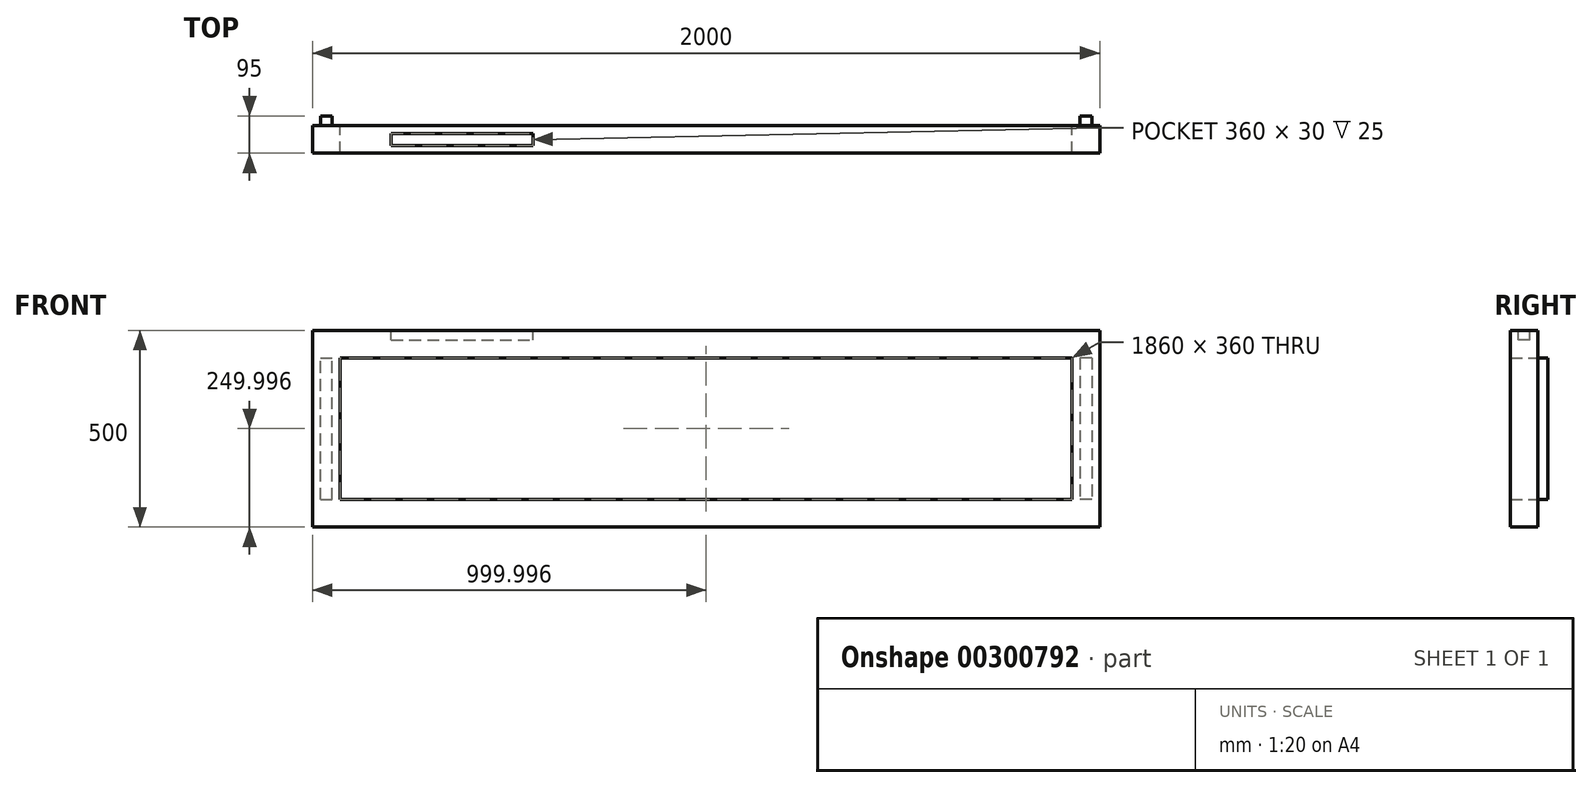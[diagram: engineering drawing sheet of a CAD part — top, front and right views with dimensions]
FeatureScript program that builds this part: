
annotation { "Feature Type Name" : "Feature", "Feature Type Description" : "" }
export const myFeature = defineFeature(function(context is Context, id is Id, definition is map)
    precondition{}
    {
        {
            var Q0;
            Q0=qCreatedBy(makeId("Front.planeOp"),FACE);
            var sketch = newSketch(context, id + "F0", { "sketchPlane" : qUnion([Q0])});
            skLineSegment(sketch, "E0.bottom", {"start": v(-981.05, -103.42) * mm, "end": v(1018.95, -103.42) * mm});
            skLineSegment(sketch, "E0.top", {"start": v(-981.05, -603.42) * mm, "end": v(1018.95, -603.42) * mm});
            skLineSegment(sketch, "E0.left", {"start": v(-981.05, -103.42) * mm, "end": v(-981.05, -603.42) * mm});
            skLineSegment(sketch, "E0.right", {"start": v(1018.95, -103.42) * mm, "end": v(1018.95, -603.42) * mm});
            skLineSegment(sketch, "E1.bottom", {"start": v(-911.05, -173.42) * mm, "end": v(948.95, -173.42) * mm});
            skLineSegment(sketch, "E1.top", {"start": v(-911.05, -533.42) * mm, "end": v(948.95, -533.42) * mm});
            skLineSegment(sketch, "E1.left", {"start": v(-911.05, -173.42) * mm, "end": v(-911.05, -533.42) * mm});
            skLineSegment(sketch, "E1.right", {"start": v(948.95, -173.42) * mm, "end": v(948.95, -533.42) * mm});
            skPoint(sketch, "E2", {"position": v(-911.05, -533.42) * mm});
            skSolve(sketch);
        }
        {
            var Q0;
            Q0=makeQuery(id+"F0.imprint","IMPRINT",FACE,{"disambiguationData":[TD([[makeQuery(id+"F0.imprint","IMPRINT",EDGE,{"derivedFrom":sQuery(id+"F0.wireOp",EDGE,"E0.bottom")}),-1.0]])]});
            extrude(context, id + "F1", {"entities" : qUnion([Q0]), "depth" : 70 * mm});
        }
        {
            var Q0;
            Q0=makeQuery(id+"F1.opExtrude","CAP_FACE",FACE,{"disambiguationData":[OSD([sQuery(id+"F0.wireOp",EDGE,"E0.bottom"),sQuery(id+"F0.wireOp",EDGE,"E0.top"),sQuery(id+"F0.wireOp",EDGE,"E0.left"),sQuery(id+"F0.wireOp",EDGE,"E0.right"),sQuery(id+"F0.wireOp",EDGE,"E1.bottom"),sQuery(id+"F0.wireOp",EDGE,"E1.top"),sQuery(id+"F0.wireOp",EDGE,"E1.left"),sQuery(id+"F0.wireOp",EDGE,"E1.right")])],"isStart":true});
            var sketch = newSketch(context, id + "F2", { "sketchPlane" : qUnion([Q0])});
            skLineSegment(sketch, "E3.bottom", {"start": v(-998.95, -173.42) * mm, "end": v(-968.95, -173.42) * mm});
            skLineSegment(sketch, "E3.top", {"start": v(-998.95, -533.42) * mm, "end": v(-968.95, -533.42) * mm});
            skLineSegment(sketch, "E3.left", {"start": v(-998.95, -173.42) * mm, "end": v(-998.95, -533.42) * mm});
            skLineSegment(sketch, "E3.right", {"start": v(-968.95, -173.42) * mm, "end": v(-968.95, -533.42) * mm});
            skLineSegment(sketch, "E4.bottom", {"start": v(931.05, -173.42) * mm, "end": v(961.05, -173.42) * mm});
            skLineSegment(sketch, "E4.top", {"start": v(931.05, -533.42) * mm, "end": v(961.05, -533.42) * mm});
            skLineSegment(sketch, "E4.left", {"start": v(931.05, -173.42) * mm, "end": v(931.05, -533.42) * mm});
            skLineSegment(sketch, "E4.right", {"start": v(961.05, -173.42) * mm, "end": v(961.05, -533.42) * mm});
            skSolve(sketch);
        }
        {
            var Q0;
            Q0=makeQuery(id+"F2.imprint","IMPRINT",FACE,{"disambiguationData":[TD([[makeQuery(id+"F2.imprint","IMPRINT",EDGE,{"derivedFrom":sQuery(id+"F2.wireOp",EDGE,"E4.bottom")}),-1.0]])]});
            extrude(context, id + "F3", {"entities" : qUnion([Q0]), "oppositeDirection" : true, "depth" : 25 * mm});
        }
        {
            var Q0;
            Q0 = qSketchRegion(id + "F2", true);
            extrude(context, id + "F4", {"entities" : qUnion([Q0]), "operationType" : NewBodyOperationType.ADD, "depth" : 25 * mm});
        }
        {
            var Q0;
            Q0=makeQuery(id+"F1.opExtrude","SWEPT_FACE",FACE,{"disambiguationData":[OSD([sQuery(id+"F0.wireOp",EDGE,"E0.bottom")])]});
            var sketch = newSketch(context, id + "F5", { "sketchPlane" : qUnion([Q0])});
            skLineSegment(sketch, "E5.bottom", {"start": v(-781.05, -20) * mm, "end": v(-421.05, -20) * mm});
            skLineSegment(sketch, "E5.top", {"start": v(-781.05, -50) * mm, "end": v(-421.05, -50) * mm});
            skLineSegment(sketch, "E5.left", {"start": v(-781.05, -20) * mm, "end": v(-781.05, -50) * mm});
            skLineSegment(sketch, "E5.right", {"start": v(-421.05, -20) * mm, "end": v(-421.05, -50) * mm});
            skSolve(sketch);
        }
        {
            var Q0;
            Q0=makeQuery(id+"F5.imprint","IMPRINT",FACE,{"disambiguationData":[TD([[makeQuery(id+"F5.imprint","IMPRINT",EDGE,{"derivedFrom":sQuery(id+"F5.wireOp",EDGE,"E5.bottom")}),-1.0]])]});
            extrude(context, id + "F6", {"entities" : qUnion([Q0]), "operationType" : NewBodyOperationType.REMOVE, "oppositeDirection" : true, "depth" : 25 * mm});
        }
    });
